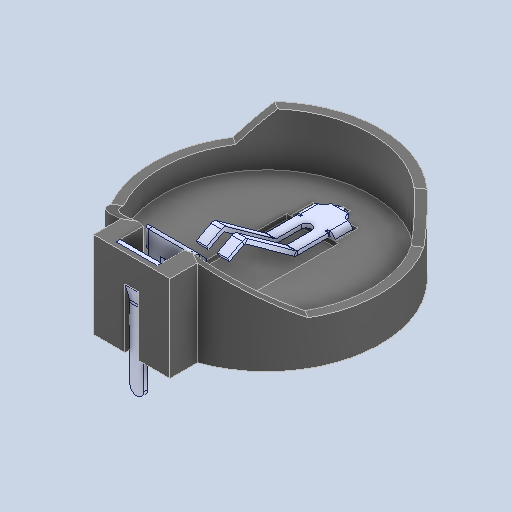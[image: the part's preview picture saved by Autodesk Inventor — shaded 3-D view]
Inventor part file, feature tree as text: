
AUTODESK INVENTOR PART (.ipt)
format: ipt  version: 2024 (Build 280153000, 153)  size: 301,568 bytes
history: native  units: mm
features: fillet x2, other x1
ambient origin geometry x8: Origin, YZ Plane, XZ Plane, XY Plane, X Axis, Y Axis, Z Axis, Center Point
bodies: Solide1 (feature_tree), Solide2 (feature_tree), Solide3 (feature_tree)
feature tree (3):
  fillet  "Fillet4"  [1 undecoded]
  fillet  "Fillet5"  [1 undecoded]
  other  "Boss-Extrude2"
note: 2 required parameter values undecoded (feature->parameter linkage not recoverable at this tier; creation-order binding heuristic only, values carry confidence <= 0.55)
